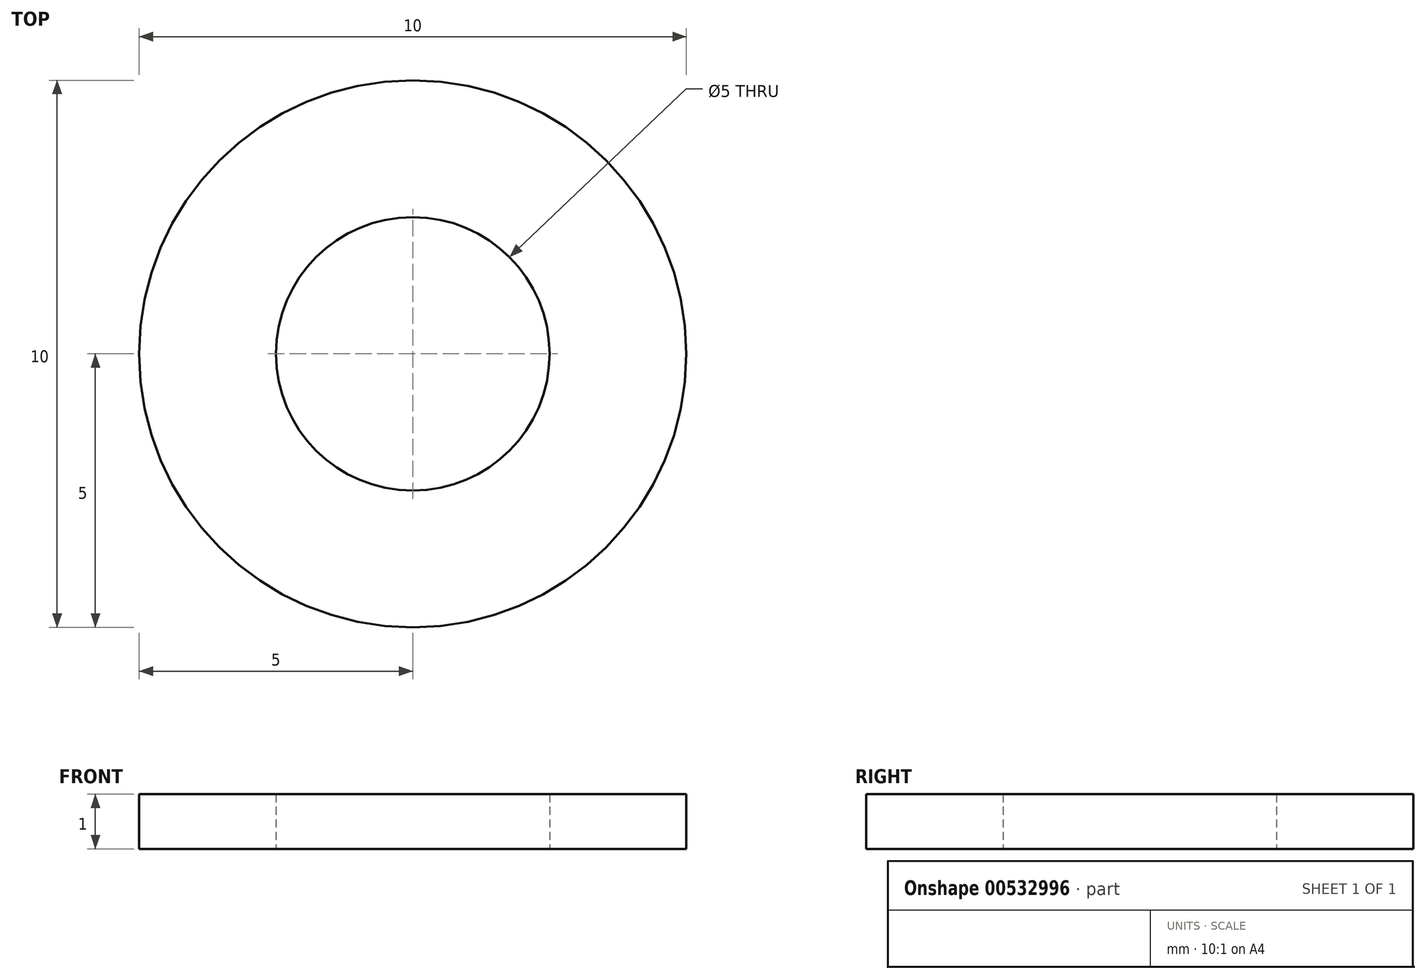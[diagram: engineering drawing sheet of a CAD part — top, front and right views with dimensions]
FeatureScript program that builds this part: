
annotation { "Feature Type Name" : "Feature", "Feature Type Description" : "" }
export const myFeature = defineFeature(function(context is Context, id is Id, definition is map)
    precondition{}
    {
        {
            var Q0;
            Q0=qCreatedBy(makeId("Top.planeOp"),FACE);
            var sketch = newSketch(context, id + "F0", { "sketchPlane" : qUnion([Q0])});
            skCircle(sketch, "E0", {"center": v(0, 0) * mm, "radius": 5 * mm});
            skCircle(sketch, "E1", {"center": v(0, 0) * mm, "radius": 2.5 * mm});
            skSolve(sketch);
        }
        {
            var Q0;
            Q0=makeQuery(id+"F0.imprint","IMPRINT",FACE,{"disambiguationData":[TD([[makeQuery(id+"F0.imprint","IMPRINT",EDGE,{"derivedFrom":sQuery(id+"F0.wireOp",EDGE,"E0")}),1.0]])]});
            extrude(context, id + "F1", {"entities" : qUnion([Q0]), "depth" : 1 * mm, "offsetDistance" : 25 * mm});
        }
    });
